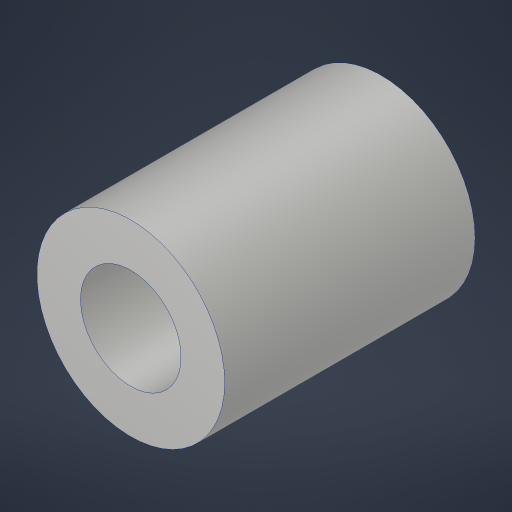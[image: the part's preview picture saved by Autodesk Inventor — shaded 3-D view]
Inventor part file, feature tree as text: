
AUTODESK INVENTOR PART (.ipt)
format: ipt  version: 2023.4 (Build 274418000, 418)  size: 168,960 bytes
history: native  units: in
note: dims shown in document units (in); Inventor stores cm internally (conversion verified against a paired STEP export)
features: extrude x1, hole x1
ambient origin geometry x8: Origin, YZ Plane, XZ Plane, XY Plane, X Axis, Y Axis, Z Axis, Center Point
bodies: Solid1 (feature_tree)
feature tree (2):
  extrude  "Extrusion1"  Depth=0.5in
  hole  "Hole1"  [1 undecoded]
note: 1 required parameter value undecoded (feature->parameter linkage not recoverable at this tier; creation-order binding heuristic only, values carry confidence <= 0.55)
